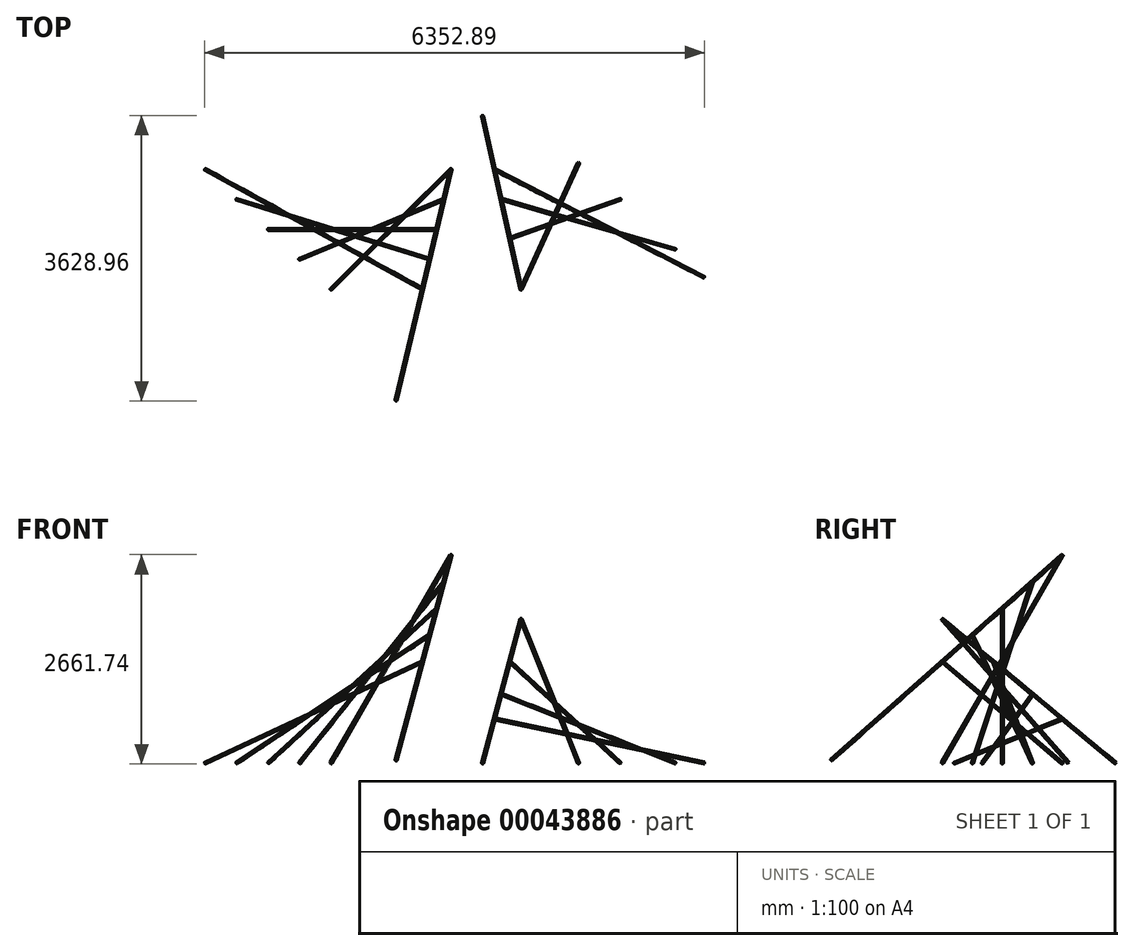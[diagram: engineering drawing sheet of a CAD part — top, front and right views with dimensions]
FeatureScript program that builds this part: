
annotation { "Feature Type Name" : "Feature", "Feature Type Description" : "" }
export const myFeature = defineFeature(function(context is Context, id is Id, definition is map)
    precondition{}
    {
        {
            var Q0;
            Q0=qCreatedBy(makeId("Front.planeOp"),FACE);
            var sketch = newSketch(context, id + "F0", { "sketchPlane" : qUnion([Q0])});
            skLineSegment(sketch, "E0", {"start": v(0, 0) * mm, "end": v(788.88, 2944.14) * mm});
            skSolve(sketch);
        }
        {
            var Q0;
            Q0=qCreatedBy(makeId("Front.planeOp"),FACE);
            cPlane(context, id + "F1", {"entities" : qUnion([Q0]), "cplaneType" : CPlaneType.OFFSET, "offset" : 1524 * mm, "oppositeDirection" : true, "width" : 152.4 * mm, "height" : 152.4 * mm});
        }
        {
            var Q0;
            Q0=qCreatedBy(id+"F1.planeOp",FACE);
            var sketch = newSketch(context, id + "F2", { "sketchPlane" : qUnion([Q0])});
            skLineSegment(sketch, "E1", {"start": v(0, 0) * mm, "end": v(788.88, 2944.14) * mm});
            skLineSegment(sketch, "E2", {"start": v(788.88, 2944.14) * mm, "end": v(522.39, 3015.55) * mm});
            skSolve(sketch);
        }
        {
            var Q0;
            Q0=qCreatedBy(id+"F1.planeOp",FACE);
            var sketch = newSketch(context, id + "F3", { "sketchPlane" : qUnion([Q0])});
            skLineSegment(sketch, "E3", {"start": v(788.88, 2944.14) * mm, "end": v(788.88, 0) * mm});
            skSolve(sketch);
        }
        {
            var Q0;
            Q0=qCreatedBy(id+"F1.planeOp",FACE);
            var sketch = newSketch(context, id + "F4", { "sketchPlane" : qUnion([Q0])});
            skLineSegment(sketch, "E4", {"start": v(788.88, 2944.14) * mm, "end": v(0, 0) * mm});
            skSolve(sketch);
        }
        {
            var Q0;
            Q0=qCreatedBy(id+"F1.planeOp",FACE);
            var sketch = newSketch(context, id + "F5", { "sketchPlane" : qUnion([Q0])});
            skLineSegment(sketch, "E5", {"start": v(345.16, 1288.14) * mm, "end": v(-2417.27, 0) * mm});
            skSolve(sketch);
        }
        {
            var Q0;
            Q0=qCreatedBy(makeId("Front.planeOp"),FACE);
            var sketch = newSketch(context, id + "F6", { "sketchPlane" : qUnion([Q0])});
            skLineSegment(sketch, "E6", {"start": v(-2417.27, 0) * mm, "end": v(345.16, 1288.14) * mm});
            skLineSegment(sketch, "E7", {"start": v(345.16, 1288.14) * mm, "end": v(246.93, 1498.78) * mm});
            skSolve(sketch);
        }
        {
            var Q0;
            Q0=qCreatedBy(makeId("Front.planeOp"),FACE);
            var sketch = newSketch(context, id + "F7", { "sketchPlane" : qUnion([Q0])});
            skLineSegment(sketch, "E8", {"start": v(707.3, 2639.65) * mm, "end": v(-816.7, 0) * mm});
            skSolve(sketch);
        }
        {
            var Q0;
            Q0=qCreatedBy(id+"F1.planeOp",FACE);
            var sketch = newSketch(context, id + "F8", { "sketchPlane" : qUnion([Q0])});
            skLineSegment(sketch, "E9", {"start": v(-816.7, 0) * mm, "end": v(707.3, 2639.65) * mm});
            skLineSegment(sketch, "E10", {"start": v(707.3, 2639.65) * mm, "end": v(435.48, 2796.58) * mm});
            skSolve(sketch);
        }
        {
            var Q0;
            Q0=qCreatedBy(makeId("Front.planeOp"),FACE);
            var sketch = newSketch(context, id + "F9", { "sketchPlane" : qUnion([Q0])});
            skLineSegment(sketch, "E11", {"start": v(345.16, 1288.14) * mm, "end": v(707.3, 2639.65) * mm});
            skPoint(sketch, "E12", {"position": v(526.22, 1963.9) * mm});
            skLineSegment(sketch, "E13", {"start": v(-816.7, 0) * mm, "end": v(-2417.27, 0) * mm});
            skPoint(sketch, "E14", {"position": v(-1616.99, 0) * mm});
            skSolve(sketch);
        }
        {
            var Q0;
            Q0=sQuery(id+"F9.wireOp",VERTEX,"E13.start");
            var Q1;
            Q1=sQuery(id+"F8.wireOp",VERTEX,"E10.start");
            var Q2;
            Q2=sQuery(id+"F8.wireOp",VERTEX,"E9.start");
            cPlane(context, id + "F10", {"entities" : qUnion([Q0, Q1, Q2]), "cplaneType" : CPlaneType.THREE_POINT, "offset" : 152.4 * mm, "width" : 152.4 * mm, "height" : 152.4 * mm});
        }
        {
            var Q0;
            Q0=qCreatedBy(id+"F10.planeOp",FACE);
            var sketch = newSketch(context, id + "F11", { "sketchPlane" : qUnion([Q0])});
            skLineSegment(sketch, "E15", {"start": v(0, -408.35) * mm, "end": v(1524, 2639.65) * mm});
            skSolve(sketch);
        }
        {
            var Q0;
            Q0=sQuery(id+"F6.wireOp",VERTEX,"E6.start");
            var Q1;
            Q1=sQuery(id+"F6.wireOp",VERTEX,"E7.start");
            var Q2;
            Q2=sQuery(id+"F5.wireOp",VERTEX,"E5.start");
            cPlane(context, id + "F12", {"entities" : qUnion([Q0, Q1, Q2]), "cplaneType" : CPlaneType.THREE_POINT, "offset" : 152.4 * mm, "width" : 152.4 * mm, "height" : 152.4 * mm});
        }
        {
            var Q0;
            Q0=qCreatedBy(id+"F12.planeOp",FACE);
            var sketch = newSketch(context, id + "F13", { "sketchPlane" : qUnion([Q0])});
            skLineSegment(sketch, "E16", {"start": v(-2190.8, -1524) * mm, "end": v(857.2, 0) * mm});
            skSolve(sketch);
        }
        {
            var Q0;
            Q0=qCreatedBy(makeId("Front.planeOp"),FACE);
            cPlane(context, id + "F14", {"entities" : qUnion([Q0]), "cplaneType" : CPlaneType.OFFSET, "offset" : 762 * mm, "oppositeDirection" : true, "width" : 152.4 * mm, "height" : 152.4 * mm});
        }
        {
            var Q0;
            Q0=qCreatedBy(id+"F14.planeOp",FACE);
            var sketch = newSketch(context, id + "F15", { "sketchPlane" : qUnion([Q0])});
            skLineSegment(sketch, "E17", {"start": v(-1616.99, 0) * mm, "end": v(526.22, 1963.9) * mm});
            skSolve(sketch);
        }
        {
            var Q0;
            Q0=qCreatedBy(makeId("Front.planeOp"),FACE);
            var sketch = newSketch(context, id + "F16", { "sketchPlane" : qUnion([Q0])});
            skLineSegment(sketch, "E18", {"start": v(526.22, 1963.9) * mm, "end": v(345.16, 1288.14) * mm});
            skLineSegment(sketch, "E19", {"start": v(526.22, 1963.9) * mm, "end": v(707.3, 2639.65) * mm});
            skLineSegment(sketch, "E20", {"start": v(-816.7, 0) * mm, "end": v(-1616.99, 0) * mm});
            skLineSegment(sketch, "E21", {"start": v(-1616.99, 0) * mm, "end": v(-2417.27, 0) * mm});
            skLineSegment(sketch, "E22", {"start": v(616.76, 2301.77) * mm, "end": v(-1216.85, 0) * mm});
            skLineSegment(sketch, "E23", {"start": v(-2017.13, 0) * mm, "end": v(435.69, 1626.02) * mm});
            skSolve(sketch);
        }
        {
            var Q0;
            Q0=sQuery(id+"F0.wireOp",VERTEX,"E0.start");
            var Q1;
            Q1=sQuery(id+"F16.wireOp",VERTEX,"E19.end");
            var Q2;
            Q2=sQuery(id+"F11.wireOp",VERTEX,"E15.end");
            cPlane(context, id + "F17", {"entities" : qUnion([Q0, Q1, Q2]), "cplaneType" : CPlaneType.THREE_POINT, "offset" : 152.4 * mm, "width" : 152.4 * mm, "height" : 152.4 * mm});
        }
        {
            var Q0;
            Q0=qCreatedBy(id+"F17.planeOp",FACE);
            var sketch = newSketch(context, id + "F18", { "sketchPlane" : qUnion([Q0])});
            skLineSegment(sketch, "E24", {"start": v(0, 0) * mm, "end": v(1524, 0) * mm});
            skLineSegment(sketch, "E25", {"start": v(0, 2382.97) * mm, "end": v(1524, 2382.97) * mm});
            skLineSegment(sketch, "E26", {"start": v(0, 1683.38) * mm, "end": v(1524, 1683.38) * mm});
            skLineSegment(sketch, "E27", {"start": v(0, 2382.97) * mm, "end": v(762, 2382.97) * mm});
            skLineSegment(sketch, "E28", {"start": v(762, 2382.97) * mm, "end": v(1524, 2382.97) * mm});
            skLineSegment(sketch, "E29", {"start": v(0, 1683.38) * mm, "end": v(762, 1683.38) * mm});
            skLineSegment(sketch, "E30", {"start": v(762, 1683.38) * mm, "end": v(1524, 1683.38) * mm});
            skPoint(sketch, "E31", {"position": v(381, 2382.97) * mm});
            skPoint(sketch, "E32", {"position": v(381, 1683.38) * mm});
            skPoint(sketch, "E33", {"position": v(1143, 2382.97) * mm});
            skPoint(sketch, "E34", {"position": v(1143, 1683.38) * mm});
            skSolve(sketch);
        }
        {
            var Q0;
            Q0=qCreatedBy(makeId("Top.planeOp"),FACE);
            var sketch = newSketch(context, id + "F19", { "sketchPlane" : qUnion([Q0])});
            skLineSegment(sketch, "E35", {"start": v(-2017.13, 0) * mm, "end": v(-2017.13, 1524) * mm});
            skLineSegment(sketch, "E36", {"start": v(-1216.85, 0) * mm, "end": v(-1216.85, 1524) * mm});
            skLineSegment(sketch, "E37", {"start": v(-2017.13, 762) * mm, "end": v(-2017.13, 1524) * mm});
            skLineSegment(sketch, "E38", {"start": v(-2017.13, 762) * mm, "end": v(-2017.13, 0) * mm});
            skLineSegment(sketch, "E39", {"start": v(-1216.85, 1524) * mm, "end": v(-1216.85, 762) * mm});
            skLineSegment(sketch, "E40", {"start": v(-1216.85, 762) * mm, "end": v(-1216.85, 0) * mm});
            skPoint(sketch, "E41", {"position": v(-1216.85, 381) * mm});
            skPoint(sketch, "E42", {"position": v(-2017.13, 381) * mm});
            skPoint(sketch, "E43", {"position": v(-2017.13, 1143) * mm});
            skPoint(sketch, "E44", {"position": v(-1216.85, 1143) * mm});
            skSolve(sketch);
        }
        {
            var Q0;
            Q0=sQuery(id+"F19.wireOp",VERTEX,"E43");
            var Q1;
            Q1=sQuery(id+"F18.wireOp",VERTEX,"E32");
            var Q2;
            Q2=sQuery(id+"F18.wireOp",VERTEX,"E34");
            cPlane(context, id + "F20", {"entities" : qUnion([Q0, Q1, Q2]), "cplaneType" : CPlaneType.THREE_POINT, "offset" : 152.4 * mm, "width" : 152.4 * mm, "height" : 152.4 * mm});
        }
        {
            var Q0;
            Q0=qCreatedBy(id+"F20.planeOp",FACE);
            var sketch = newSketch(context, id + "F21", { "sketchPlane" : qUnion([Q0])});
            skLineSegment(sketch, "E45", {"start": v(-1681.26, -1143) * mm, "end": v(1261.57, -381) * mm});
            skSolve(sketch);
        }
        {
            var Q0;
            Q0=sQuery(id+"F19.wireOp",VERTEX,"E41");
            var Q1;
            Q1=sQuery(id+"F18.wireOp",VERTEX,"E33");
            var Q2;
            Q2=sQuery(id+"F18.wireOp",VERTEX,"E31");
            cPlane(context, id + "F22", {"entities" : qUnion([Q0, Q1, Q2]), "cplaneType" : CPlaneType.THREE_POINT, "offset" : 152.4 * mm, "width" : 152.4 * mm, "height" : 152.4 * mm});
        }
        {
            var Q0;
            Q0=qCreatedBy(id+"F22.planeOp",FACE);
            var sketch = newSketch(context, id + "F23", { "sketchPlane" : qUnion([Q0])});
            skLineSegment(sketch, "E46", {"start": v(-381, -758.19) * mm, "end": v(-1143, 2184.64) * mm});
            skSolve(sketch);
        }
        {
            var Q0;
            Q0=sQuery(id+"F13.wireOp",VERTEX,"E16.end");
            var Q1;
            Q1=sQuery(id+"F11.wireOp",VERTEX,"E15.end");
            var Q2;
            Q2=sQuery(id+"F15.wireOp",VERTEX,"E17.start");
            cPlane(context, id + "F24", {"entities" : qUnion([Q0, Q1, Q2]), "cplaneType" : CPlaneType.THREE_POINT, "offset" : 152.4 * mm, "width" : 152.4 * mm, "height" : 152.4 * mm});
        }
        {
            var Q0;
            Q0=qCreatedBy(id+"F24.planeOp",FACE);
            var sketch = newSketch(context, id + "F25", { "sketchPlane" : qUnion([Q0])});
            skLineSegment(sketch, "E47", {"start": v(1378.45, -2734.5) * mm, "end": v(501.73, 1152.57) * mm});
            skSolve(sketch);
        }
        {
            var Q0;
            Q0=sQuery(id+"F11.wireOp",EDGE,"E15");
            cPlane(context, id + "F26", {"entities" : qUnion([Q0]), "cplaneType" : CPlaneType.MID_PLANE, "offset" : 152.4 * mm, "oppositeDirection" : true, "width" : 152.4 * mm, "height" : 152.4 * mm});
        }
        {
            var Q0;
            Q0=qCreatedBy(makeId("Top.planeOp"),FACE);
            var sketch = newSketch(context, id + "F27", { "sketchPlane" : qUnion([Q0])});
            skLineSegment(sketch, "E48", {"start": v(707.3, 1524) * mm, "end": v(345.16, 0) * mm});
            skLineSegment(sketch, "E49", {"start": v(707.3, 1524) * mm, "end": v(707.3, 0) * mm});
            skLineSegment(sketch, "E50.0", {"start": v(1469.3, 1524) * mm, "end": v(1469.3, 0) * mm});
            skLineSegment(sketch, "E51", {"start": v(1469.3, 1524) * mm, "end": v(1107.15, 0) * mm});
            skLineSegment(sketch, "E52", {"start": v(1469.3, 1524) * mm, "end": v(4234.33, 0) * mm});
            skSolve(sketch);
        }
        {
            var Q0;
            Q0=qCreatedBy(makeId("Front.planeOp"),FACE);
            var sketch = newSketch(context, id + "F28", { "sketchPlane" : qUnion([Q0])});
            skLineSegment(sketch, "E53", {"start": v(1469.3, 0) * mm, "end": v(4234.33, 0) * mm});
            skLineSegment(sketch, "E54.0", {"start": v(1469.3, 1828.8) * mm, "end": v(4234.33, 1828.8) * mm});
            skSolve(sketch);
        }
        {
            var Q0;
            Q0=qCreatedBy(makeId("Top.planeOp"),FACE);
            cPlane(context, id + "F29", {"entities" : qUnion([Q0]), "cplaneType" : CPlaneType.OFFSET, "offset" : 1828.8 * mm, "width" : 152.4 * mm, "height" : 152.4 * mm});
        }
        {
            var Q0;
            Q0=qCreatedBy(id+"F29.planeOp",FACE);
            var sketch = newSketch(context, id + "F30", { "sketchPlane" : qUnion([Q0])});
            skLineSegment(sketch, "E55", {"start": v(1469.3, 1524) * mm, "end": v(4234.33, 0) * mm});
            skSolve(sketch);
        }
        {
            var Q0;
            Q0=qCreatedBy(makeId("Front.planeOp"),FACE);
            var sketch = newSketch(context, id + "F31", { "sketchPlane" : qUnion([Q0])});
            skLineSegment(sketch, "E56", {"start": v(1107.15, 0) * mm, "end": v(1597.18, 1828.8) * mm});
            skLineSegment(sketch, "E57", {"start": v(1107.15, 0) * mm, "end": v(4221.7, 0) * mm});
            skLineSegment(sketch, "E58", {"start": v(4221.7, 0) * mm, "end": v(1257.92, 562.7) * mm});
            skLineSegment(sketch, "E59", {"start": v(3557.9, 0) * mm, "end": v(1352.16, 914.4) * mm});
            skLineSegment(sketch, "E60", {"start": v(2859.49, 0) * mm, "end": v(1452.5, 1288.87) * mm});
            skLineSegment(sketch, "E61", {"start": v(2259.2, 0) * mm, "end": v(1597.18, 1828.8) * mm});
            skSolve(sketch);
        }
        {
            var Q0;
            Q0=qCreatedBy(makeId("Top.planeOp"),FACE);
            var sketch = newSketch(context, id + "F32", { "sketchPlane" : qUnion([Q0])});
            skLineSegment(sketch, "E62", {"start": v(1597.18, 0) * mm, "end": v(1597.18, 1453.51) * mm});
            skSolve(sketch);
        }
        {
            var Q0;
            Q0=qCreatedBy(makeId("Top.planeOp"),FACE);
            var sketch = newSketch(context, id + "F33", { "sketchPlane" : qUnion([Q0])});
            skLineSegment(sketch, "E63", {"start": v(2259.2, 0) * mm, "end": v(1597.18, 1453.51) * mm});
            skSolve(sketch);
        }
        {
            var Q0;
            Q0=qCreatedBy(id+"F29.planeOp",FACE);
            var sketch = newSketch(context, id + "F34", { "sketchPlane" : qUnion([Q0])});
            skLineSegment(sketch, "E64", {"start": v(2259.2, 0) * mm, "end": v(1597.18, 1453.51) * mm});
            skSolve(sketch);
        }
        {
            var Q0;
            Q0=qCreatedBy(makeId("Top.planeOp"),FACE);
            var sketch = newSketch(context, id + "F35", { "sketchPlane" : qUnion([Q0])});
            skLineSegment(sketch, "E65", {"start": v(4221.7, 0) * mm, "end": v(4221.7, 1444.78) * mm});
            skLineSegment(sketch, "E66", {"start": v(1597.18, 1453.51) * mm, "end": v(4221.7, 1444.78) * mm});
            skSolve(sketch);
        }
        {
            var Q0;
            Q0=qCreatedBy(makeId("Top.planeOp"),FACE);
            var sketch = newSketch(context, id + "F36", { "sketchPlane" : qUnion([Q0])});
            skLineSegment(sketch, "E67", {"start": v(1257.92, 0) * mm, "end": v(4221.7, 1444.78) * mm});
            skSolve(sketch);
        }
        {
            var Q0;
            Q0=qCreatedBy(makeId("Top.planeOp"),FACE);
            var sketch = newSketch(context, id + "F37", { "sketchPlane" : qUnion([Q0])});
            skLineSegment(sketch, "E68", {"start": v(1257.92, 0) * mm, "end": v(1257.92, 1524) * mm});
            skLineSegment(sketch, "E69", {"start": v(1257.92, 1524) * mm, "end": v(4221.7, 0) * mm});
            skSolve(sketch);
        }
        {
            var Q0;
            Q0=qCreatedBy(id+"F29.planeOp",FACE);
            var sketch = newSketch(context, id + "F38", { "sketchPlane" : qUnion([Q0])});
            skLineSegment(sketch, "E70", {"start": v(1257.92, 1524) * mm, "end": v(4221.7, 0) * mm});
            skSolve(sketch);
        }
        {
            var Q0;
            Q0=sQuery(id+"F37.wireOp",VERTEX,"E69.end");
            var Q1;
            Q1=sQuery(id+"F37.wireOp",VERTEX,"E69.start");
            var Q2;
            Q2=sQuery(id+"F38.wireOp",VERTEX,"E70.start");
            cPlane(context, id + "F39", {"entities" : qUnion([Q0, Q1, Q2]), "cplaneType" : CPlaneType.THREE_POINT, "offset" : 152.4 * mm, "width" : 152.4 * mm, "height" : 152.4 * mm});
        }
        {
            var Q0;
            Q0=qCreatedBy(id+"F39.planeOp",FACE);
            var sketch = newSketch(context, id + "F40", { "sketchPlane" : qUnion([Q0])});
            skLineSegment(sketch, "E71", {"start": v(3417.44, 0) * mm, "end": v(421.77, 562.4) * mm});
            skSolve(sketch);
        }
        {
            var Q0;
            Q0=qCreatedBy(makeId("Top.planeOp"),FACE);
            var sketch = newSketch(context, id + "F41", { "sketchPlane" : qUnion([Q0])});
            skLineSegment(sketch, "E72", {"start": v(2259.2, 0) * mm, "end": v(2259.2, 1451.31) * mm});
            skSolve(sketch);
        }
        {
            var Q0;
            Q0=sQuery(id+"F41.wireOp",VERTEX,"E72.end");
            var Q1;
            Q1=sQuery(id+"F31.wireOp",VERTEX,"E61.end");
            var Q2;
            Q2=sQuery(id+"F32.wireOp",VERTEX,"E62.start");
            cPlane(context, id + "F42", {"entities" : qUnion([Q0, Q1, Q2]), "cplaneType" : CPlaneType.THREE_POINT, "offset" : 152.4 * mm, "width" : 152.4 * mm, "height" : 152.4 * mm});
        }
        {
            var Q0;
            Q0=qCreatedBy(id+"F42.planeOp",FACE);
            var sketch = newSketch(context, id + "F43", { "sketchPlane" : qUnion([Q0])});
            skLineSegment(sketch, "E73", {"start": v(-2425.54, 0) * mm, "end": v(-662.85, 1828.8) * mm});
            skSolve(sketch);
        }
        {
            var Q0;
            Q0=qCreatedBy(makeId("Top.planeOp"),FACE);
            var sketch = newSketch(context, id + "F44", { "sketchPlane" : qUnion([Q0])});
            skLineSegment(sketch, "E74", {"start": v(1107.15, 0) * mm, "end": v(1107.15, 1524) * mm});
            skLineSegment(sketch, "E75", {"start": v(1257.92, 0) * mm, "end": v(1257.92, 1524) * mm});
            skLineSegment(sketch, "E76", {"start": v(1352.16, 0) * mm, "end": v(1352.16, 1143) * mm});
            skLineSegment(sketch, "E77", {"start": v(1452.5, 0) * mm, "end": v(1452.5, 381) * mm});
            skLineSegment(sketch, "E78", {"start": v(3557.9, 0) * mm, "end": v(3557.9, 508) * mm});
            skLineSegment(sketch, "E79", {"start": v(2859.49, 0) * mm, "end": v(2859.49, 1143) * mm});
            skLineSegment(sketch, "E80", {"start": v(3557.9, 508) * mm, "end": v(1352.16, 1143) * mm});
            skLineSegment(sketch, "E81", {"start": v(2859.49, 1143) * mm, "end": v(1452.5, 381) * mm});
            skSolve(sketch);
        }
        {
            var Q0;
            Q0=qCreatedBy(id+"F29.planeOp",FACE);
            var sketch = newSketch(context, id + "F45", { "sketchPlane" : qUnion([Q0])});
            skLineSegment(sketch, "E82", {"start": v(2859.49, 1143) * mm, "end": v(1452.5, 381) * mm});
            skLineSegment(sketch, "E83", {"start": v(3557.9, 508) * mm, "end": v(1352.16, 1143) * mm});
            skSolve(sketch);
        }
        {
            var Q0;
            Q0=sQuery(id+"F45.wireOp",VERTEX,"E82.start");
            var Q1;
            Q1=sQuery(id+"F45.wireOp",VERTEX,"E82.end");
            var Q2;
            Q2=sQuery(id+"F44.wireOp",VERTEX,"E81.end");
            cPlane(context, id + "F46", {"entities" : qUnion([Q0, Q1, Q2]), "cplaneType" : CPlaneType.THREE_POINT, "offset" : 152.4 * mm, "width" : 152.4 * mm, "height" : 152.4 * mm});
        }
        {
            var Q0;
            Q0=sQuery(id+"F31.wireOp",VERTEX,"E60.end");
            var Q1;
            Q1=qCreatedBy(makeId("Top.planeOp"),FACE);
            cPlane(context, id + "F47", {"entities" : qUnion([Q0, Q1]), "cplaneType" : CPlaneType.PLANE_POINT, "offset" : 152.4 * mm, "width" : 152.4 * mm, "height" : 152.4 * mm});
        }
        {
            var Q0;
            Q0=qCreatedBy(id+"F47.planeOp",FACE);
            var sketch = newSketch(context, id + "F48", { "sketchPlane" : qUnion([Q0])});
            skLineSegment(sketch, "E84", {"start": v(1452.5, 0) * mm, "end": v(1452.5, 381) * mm});
            skSolve(sketch);
        }
        {
            var Q0;
            Q0=qCreatedBy(id+"F46.planeOp",FACE);
            var sketch = newSketch(context, id + "F49", { "sketchPlane" : qUnion([Q0])});
            skLineSegment(sketch, "E85", {"start": v(-3058.74, 0) * mm, "end": v(-1458.66, 1288.87) * mm});
            skSolve(sketch);
        }
        {
            var Q0;
            Q0=sQuery(id+"F31.wireOp",VERTEX,"E59.end");
            var Q1;
            Q1=qCreatedBy(makeId("Top.planeOp"),FACE);
            cPlane(context, id + "F50", {"entities" : qUnion([Q0, Q1]), "cplaneType" : CPlaneType.PLANE_POINT, "offset" : 152.4 * mm, "width" : 152.4 * mm, "height" : 152.4 * mm});
        }
        {
            var Q0;
            Q0=qCreatedBy(id+"F50.planeOp",FACE);
            var sketch = newSketch(context, id + "F51", { "sketchPlane" : qUnion([Q0])});
            skLineSegment(sketch, "E86", {"start": v(1352.16, 1143) * mm, "end": v(1352.16, 0) * mm});
            skSolve(sketch);
        }
        {
            var Q0;
            Q0=sQuery(id+"F44.wireOp",VERTEX,"E80.start");
            var Q1;
            Q1=sQuery(id+"F44.wireOp",VERTEX,"E80.end");
            var Q2;
            Q2=sQuery(id+"F51.wireOp",VERTEX,"E86.start");
            cPlane(context, id + "F52", {"entities" : qUnion([Q0, Q1, Q2]), "cplaneType" : CPlaneType.THREE_POINT, "offset" : 152.4 * mm, "width" : 152.4 * mm, "height" : 152.4 * mm});
        }
        {
            var Q0;
            Q0=qCreatedBy(id+"F52.planeOp",FACE);
            var sketch = newSketch(context, id + "F53", { "sketchPlane" : qUnion([Q0])});
            skLineSegment(sketch, "E87", {"start": v(3278.5, 0) * mm, "end": v(983.18, 914.4) * mm});
            skSolve(sketch);
        }
        {
            var Q0;
            Q0=sQuery(id+"F31.wireOp",VERTEX,"E56.start");
            var Q1;
            Q1=sQuery(id+"F43.wireOp",VERTEX,"E73.end");
            var Q2;
            Q2=sQuery(id+"F40.wireOp",VERTEX,"E71.end");
            cPlane(context, id + "F54", {"entities" : qUnion([Q0, Q1, Q2]), "cplaneType" : CPlaneType.THREE_POINT, "offset" : 152.4 * mm, "width" : 152.4 * mm, "height" : 152.4 * mm});
        }
        {
            var Q0;
            Q0=qCreatedBy(id+"F54.planeOp",FACE);
            var sketch = newSketch(context, id + "F55", { "sketchPlane" : qUnion([Q0])});
            skLineSegment(sketch, "E88", {"start": v(0.05, 2179.86) * mm, "end": v(2200.88, 286.55) * mm});
            skLineSegment(sketch, "E89", {"start": v(0.05, 286.55) * mm, "end": v(2200.88, 286.55) * mm});
            skSolve(sketch);
        }
        {
            var Q0;
            Q0=sQuery(id+"F49.wireOp",VERTEX,"E85.end");
            var Q1;
            Q1=qCreatedBy(makeId("Top.planeOp"),FACE);
            cPlane(context, id + "F56", {"entities" : qUnion([Q0, Q1]), "cplaneType" : CPlaneType.PLANE_POINT, "offset" : 152.4 * mm, "width" : 152.4 * mm, "height" : 152.4 * mm});
        }
        {
            var Q0;
            Q0=qCreatedBy(id+"F56.planeOp",FACE);
            var sketch = newSketch(context, id + "F57", { "sketchPlane" : qUnion([Q0])});
            skLineSegment(sketch, "E90", {"start": v(1452.5, 381) * mm, "end": v(1452.5, 649.9) * mm});
            skSolve(sketch);
        }
        {
            var Q0;
            Q0=sQuery(id+"F57.wireOp",VERTEX,"E90.end");
            var Q1;
            Q1=qCreatedBy(makeId("Front.planeOp"),FACE);
            cPlane(context, id + "F58", {"entities" : qUnion([Q0, Q1]), "cplaneType" : CPlaneType.PLANE_POINT, "offset" : 152.4 * mm, "width" : 152.4 * mm, "height" : 152.4 * mm});
        }
        {
            var Q0;
            Q0=qCreatedBy(id+"F58.planeOp",FACE);
            var sketch = newSketch(context, id + "F59", { "sketchPlane" : qUnion([Q0])});
            skLineSegment(sketch, "E91", {"start": v(1452.5, 1288.87) * mm, "end": v(1452.5, 0) * mm});
            skSolve(sketch);
        }
        {
            var Q0;
            Q0=sQuery(id+"F59.wireOp",VERTEX,"E91.start");
            var Q1;
            Q1=sQuery(id+"F59.wireOp",VERTEX,"E91.end");
            var Q2;
            Q2=sQuery(id+"F49.wireOp",VERTEX,"E85.start");
            cPlane(context, id + "F60", {"entities" : qUnion([Q0, Q1, Q2]), "cplaneType" : CPlaneType.THREE_POINT, "offset" : 152.4 * mm, "width" : 152.4 * mm, "height" : 152.4 * mm});
        }
        {
            var Q0;
            Q0=qCreatedBy(id+"F60.planeOp",FACE);
            var sketch = newSketch(context, id + "F61", { "sketchPlane" : qUnion([Q0])});
            skLineSegment(sketch, "E92", {"start": v(-1585.7, 1288.87) * mm, "end": v(-3076.6, 0) * mm});
            skSolve(sketch);
        }
        {
            var Q0;
            Q0=sQuery(id+"F25.wireOp",EDGE,"E47");
            var Q1;
            Q1=sQuery(id+"F25.wireOp",VERTEX,"E47.start");
            cPlane(context, id + "F62", {"entities" : qUnion([Q0, Q1]), "cplaneType" : CPlaneType.LINE_POINT, "offset" : 152.4 * mm, "width" : 152.4 * mm, "height" : 152.4 * mm});
        }
        {
            var Q0;
            Q0=qCreatedBy(id+"F62.planeOp",FACE);
            var sketch = newSketch(context, id + "F63", { "sketchPlane" : qUnion([Q0])});
            skCircle(sketch, "E93", {"center": v(190.23, 963.76) * mm, "radius": 12.7 * mm});
            skSolve(sketch);
        }
        {
            var Q0;
            Q0=makeQuery(id+"F63.imprint","IMPRINT",FACE,{"disambiguationData":[TD([[makeQuery(id+"F63.imprint","IMPRINT",EDGE,{"derivedFrom":sQuery(id+"F63.wireOp",EDGE,"E93")}),1.0]])]});
            var Q1;
            Q1=sQuery(id+"F25.wireOp",EDGE,"E47");
            sweep(context, id + "F64", {"profiles" : qUnion([Q0]), "path" : qUnion([Q1])});
        }
        {
            var Q0;
            Q0=sQuery(id+"F55.wireOp",EDGE,"E88");
            cPlane(context, id + "F65", {"entities" : qUnion([Q0]), "cplaneType" : CPlaneType.LINE_ANGLE, "offset" : 152.4 * mm, "angle" : 90 * degree, "width" : 152.4 * mm, "height" : 152.4 * mm});
        }
        {
            var Q0;
            Q0=qCreatedBy(id+"F65.planeOp",FACE);
            var sketch = newSketch(context, id + "F66", { "sketchPlane" : qUnion([Q0])});
            skLineSegment(sketch, "E94", {"start": v(-180.25, 1991.68) * mm, "end": v(2039.35, 120.41) * mm});
            skSolve(sketch);
        }
        {
            var Q0;
            Q0=sQuery(id+"F53.wireOp",EDGE,"E87");
            cPlane(context, id + "F67", {"entities" : qUnion([Q0]), "cplaneType" : CPlaneType.LINE_ANGLE, "offset" : 152.4 * mm, "angle" : 0 * degree, "width" : 152.4 * mm, "height" : 152.4 * mm});
        }
        {
            var Q0;
            Q0=qCreatedBy(id+"F67.planeOp",FACE);
            var sketch = newSketch(context, id + "F68", { "sketchPlane" : qUnion([Q0])});
            skLineSegment(sketch, "E95", {"start": v(3278.5, 0) * mm, "end": v(972.7, 876.59) * mm});
            skSolve(sketch);
        }
        {
            var Q0;
            Q0=sQuery(id+"F13.wireOp",EDGE,"E16");
            var Q1;
            Q1=sQuery(id+"F13.wireOp",VERTEX,"E16.end");
            cPlane(context, id + "F69", {"entities" : qUnion([Q0, Q1]), "cplaneType" : CPlaneType.LINE_POINT, "offset" : 152.4 * mm, "width" : 152.4 * mm, "height" : 152.4 * mm});
        }
        {
            var Q0;
            Q0=qCreatedBy(id+"F69.planeOp",FACE);
            var sketch = newSketch(context, id + "F70", { "sketchPlane" : qUnion([Q0])});
            skCircle(sketch, "E96", {"center": v(383.36, 1021.58) * mm, "radius": 12.7 * mm});
            skSolve(sketch);
        }
        {
            var Q0;
            Q0=makeQuery(id+"F70.imprint","IMPRINT",FACE,{"disambiguationData":[TD([[makeQuery(id+"F70.imprint","IMPRINT",EDGE,{"derivedFrom":sQuery(id+"F70.wireOp",EDGE,"E96")}),1.0]])]});
            var Q1;
            Q1=sQuery(id+"F13.wireOp",EDGE,"E16");
            sweep(context, id + "F71", {"profiles" : qUnion([Q0]), "path" : qUnion([Q1])});
        }
        {
            var Q0;
            Q0=sQuery(id+"F21.wireOp",EDGE,"E45");
            var Q1;
            Q1=sQuery(id+"F21.wireOp",VERTEX,"E45.end");
            cPlane(context, id + "F72", {"entities" : qUnion([Q0, Q1]), "cplaneType" : CPlaneType.LINE_POINT, "offset" : 152.4 * mm, "width" : 152.4 * mm, "height" : 152.4 * mm});
        }
        {
            var Q0;
            Q0=qCreatedBy(id+"F72.planeOp",FACE);
            var sketch = newSketch(context, id + "F73", { "sketchPlane" : qUnion([Q0])});
            skCircle(sketch, "E97", {"center": v(685.07, 1114.53) * mm, "radius": 12.7 * mm});
            skSolve(sketch);
        }
        {
            var Q0;
            Q0=makeQuery(id+"F73.imprint","IMPRINT",FACE,{"disambiguationData":[TD([[makeQuery(id+"F73.imprint","IMPRINT",EDGE,{"derivedFrom":sQuery(id+"F73.wireOp",EDGE,"E97")}),1.0]])]});
            var Q1;
            Q1=sQuery(id+"F21.wireOp",EDGE,"E45");
            sweep(context, id + "F74", {"profiles" : qUnion([Q0]), "path" : qUnion([Q1])});
        }
        {
            var Q0;
            Q0=sQuery(id+"F15.wireOp",EDGE,"E17");
            var Q1;
            Q1=sQuery(id+"F15.wireOp",VERTEX,"E17.end");
            cPlane(context, id + "F75", {"entities" : qUnion([Q0, Q1]), "cplaneType" : CPlaneType.LINE_POINT, "offset" : 152.4 * mm, "width" : 152.4 * mm, "height" : 152.4 * mm});
        }
        {
            var Q0;
            Q0=qCreatedBy(id+"F75.planeOp",FACE);
            var sketch = newSketch(context, id + "F76", { "sketchPlane" : qUnion([Q0])});
            skCircle(sketch, "E98", {"center": v(762, 1092.42) * mm, "radius": 12.7 * mm});
            skSolve(sketch);
        }
        {
            var Q0;
            Q0=makeQuery(id+"F76.imprint","IMPRINT",FACE,{"disambiguationData":[TD([[makeQuery(id+"F76.imprint","IMPRINT",EDGE,{"derivedFrom":sQuery(id+"F76.wireOp",EDGE,"E98")}),1.0]])]});
            var Q1;
            Q1=sQuery(id+"F15.wireOp",EDGE,"E17");
            sweep(context, id + "F77", {"profiles" : qUnion([Q0]), "path" : qUnion([Q1])});
        }
        {
            var Q0;
            Q0=sQuery(id+"F23.wireOp",EDGE,"E46");
            var Q1;
            Q1=sQuery(id+"F23.wireOp",VERTEX,"E46.end");
            cPlane(context, id + "F78", {"entities" : qUnion([Q0, Q1]), "cplaneType" : CPlaneType.LINE_POINT, "offset" : 152.4 * mm, "width" : 152.4 * mm, "height" : 152.4 * mm});
        }
        {
            var Q0;
            Q0=qCreatedBy(id+"F78.planeOp",FACE);
            var sketch = newSketch(context, id + "F79", { "sketchPlane" : qUnion([Q0])});
            skCircle(sketch, "E99", {"center": v(-1042.79, 361.7) * mm, "radius": 12.7 * mm});
            skSolve(sketch);
        }
        {
            var Q0;
            Q0=makeQuery(id+"F79.imprint","IMPRINT",FACE,{"disambiguationData":[TD([[makeQuery(id+"F79.imprint","IMPRINT",EDGE,{"derivedFrom":sQuery(id+"F79.wireOp",EDGE,"E99")}),1.0]])]});
            var Q1;
            Q1=sQuery(id+"F23.wireOp",EDGE,"E46");
            sweep(context, id + "F80", {"profiles" : qUnion([Q0]), "path" : qUnion([Q1])});
        }
        {
            var Q0;
            Q0=sQuery(id+"F11.wireOp",EDGE,"E15");
            var Q1;
            Q1=sQuery(id+"F11.wireOp",VERTEX,"E15.end");
            cPlane(context, id + "F81", {"entities" : qUnion([Q0, Q1]), "cplaneType" : CPlaneType.LINE_POINT, "offset" : 152.4 * mm, "width" : 152.4 * mm, "height" : 152.4 * mm});
        }
        {
            var Q0;
            Q0=qCreatedBy(id+"F81.planeOp",FACE);
            var sketch = newSketch(context, id + "F82", { "sketchPlane" : qUnion([Q0])});
            skCircle(sketch, "E100", {"center": v(-730.49, 0) * mm, "radius": 12.7 * mm});
            skSolve(sketch);
        }
        {
            var Q0;
            Q0=makeQuery(id+"F82.imprint","IMPRINT",FACE,{"disambiguationData":[TD([[makeQuery(id+"F82.imprint","IMPRINT",EDGE,{"derivedFrom":sQuery(id+"F82.wireOp",EDGE,"E100")}),1.0]])]});
            var Q1;
            Q1=sQuery(id+"F11.wireOp",EDGE,"E15");
            sweep(context, id + "F83", {"profiles" : qUnion([Q0]), "path" : qUnion([Q1])});
        }
        {
            var Q0;
            Q0=sQuery(id+"F66.wireOp",EDGE,"E94");
            var Q1;
            Q1=sQuery(id+"F43.wireOp",VERTEX,"E73.end");
            cPlane(context, id + "F84", {"entities" : qUnion([Q0, Q1]), "cplaneType" : CPlaneType.LINE_POINT, "offset" : 152.4 * mm, "width" : 152.4 * mm, "height" : 152.4 * mm});
        }
        {
            var Q0;
            Q0=qCreatedBy(id+"F84.planeOp",FACE);
            var sketch = newSketch(context, id + "F85", { "sketchPlane" : qUnion([Q0])});
            skCircle(sketch, "E101", {"center": v(-1377.03, 1406.55) * mm, "radius": 12.7 * mm});
            skSolve(sketch);
        }
        {
            var Q0;
            Q0=makeQuery(id+"F85.imprint","IMPRINT",FACE,{"disambiguationData":[TD([[makeQuery(id+"F85.imprint","IMPRINT",EDGE,{"derivedFrom":sQuery(id+"F85.wireOp",EDGE,"E101")}),1.0]])]});
            var Q1;
            Q1=sQuery(id+"F66.wireOp",EDGE,"E94");
            sweep(context, id + "F86", {"profiles" : qUnion([Q0]), "path" : qUnion([Q1])});
        }
        {
            var Q0;
            Q0=sQuery(id+"F43.wireOp",EDGE,"E73");
            var Q1;
            Q1=sQuery(id+"F43.wireOp",VERTEX,"E73.end");
            cPlane(context, id + "F87", {"entities" : qUnion([Q0, Q1]), "cplaneType" : CPlaneType.LINE_POINT, "offset" : 152.4 * mm, "width" : 152.4 * mm, "height" : 152.4 * mm});
        }
        {
            var Q0;
            Q0=qCreatedBy(id+"F87.planeOp",FACE);
            var sketch = newSketch(context, id + "F88", { "sketchPlane" : qUnion([Q0])});
            skCircle(sketch, "E102", {"center": v(1925.51, 1205.77) * mm, "radius": 12.7 * mm});
            skSolve(sketch);
        }
        {
            var Q0;
            Q0=makeQuery(id+"F88.imprint","IMPRINT",FACE,{"disambiguationData":[TD([[makeQuery(id+"F88.imprint","IMPRINT",EDGE,{"derivedFrom":sQuery(id+"F88.wireOp",EDGE,"E102")}),1.0]])]});
            var Q1;
            Q1=sQuery(id+"F43.wireOp",EDGE,"E73");
            sweep(context, id + "F89", {"profiles" : qUnion([Q0]), "path" : qUnion([Q1])});
        }
        {
            var Q0;
            Q0=sQuery(id+"F61.wireOp",EDGE,"E92");
            var Q1;
            Q1=sQuery(id+"F61.wireOp",VERTEX,"E92.start");
            cPlane(context, id + "F90", {"entities" : qUnion([Q0, Q1]), "cplaneType" : CPlaneType.LINE_POINT, "offset" : 152.4 * mm, "width" : 152.4 * mm, "height" : 152.4 * mm});
        }
        {
            var Q0;
            Q0=qCreatedBy(id+"F90.planeOp",FACE);
            var sketch = newSketch(context, id + "F91", { "sketchPlane" : qUnion([Q0])});
            skCircle(sketch, "E103", {"center": v(579.08, 1931.52) * mm, "radius": 12.7 * mm});
            skSolve(sketch);
        }
        {
            var Q0;
            Q0=makeQuery(id+"F91.imprint","IMPRINT",FACE,{"disambiguationData":[TD([[makeQuery(id+"F91.imprint","IMPRINT",EDGE,{"derivedFrom":sQuery(id+"F91.wireOp",EDGE,"E103")}),1.0]])]});
            var Q1;
            Q1=sQuery(id+"F61.wireOp",EDGE,"E92");
            sweep(context, id + "F92", {"profiles" : qUnion([Q0]), "path" : qUnion([Q1])});
        }
        {
            var Q0;
            Q0=sQuery(id+"F68.wireOp",EDGE,"E95");
            var Q1;
            Q1=sQuery(id+"F68.wireOp",VERTEX,"E95.end");
            cPlane(context, id + "F93", {"entities" : qUnion([Q0, Q1]), "cplaneType" : CPlaneType.LINE_POINT, "offset" : 152.4 * mm, "width" : 152.4 * mm, "height" : 152.4 * mm});
        }
        {
            var Q0;
            Q0=qCreatedBy(id+"F93.planeOp",FACE);
            var sketch = newSketch(context, id + "F94", { "sketchPlane" : qUnion([Q0])});
            skCircle(sketch, "E104", {"center": v(-1346.26, 1308.83) * mm, "radius": 12.7 * mm});
            skSolve(sketch);
        }
        {
            var Q0;
            Q0=makeQuery(id+"F94.imprint","IMPRINT",FACE,{"disambiguationData":[TD([[makeQuery(id+"F94.imprint","IMPRINT",EDGE,{"derivedFrom":sQuery(id+"F94.wireOp",EDGE,"E104")}),1.0]])]});
            var Q1;
            Q1=sQuery(id+"F68.wireOp",EDGE,"E95");
            sweep(context, id + "F95", {"profiles" : qUnion([Q0]), "path" : qUnion([Q1])});
        }
        {
            var Q0;
            Q0=sQuery(id+"F40.wireOp",EDGE,"E71");
            var Q1;
            Q1=sQuery(id+"F40.wireOp",VERTEX,"E71.end");
            cPlane(context, id + "F96", {"entities" : qUnion([Q0, Q1]), "cplaneType" : CPlaneType.LINE_POINT, "offset" : 152.4 * mm, "width" : 152.4 * mm, "height" : 152.4 * mm});
        }
        {
            var Q0;
            Q0=qCreatedBy(id+"F96.planeOp",FACE);
            var sketch = newSketch(context, id + "F97", { "sketchPlane" : qUnion([Q0])});
            skCircle(sketch, "E105", {"center": v(-1862.37, 810.1) * mm, "radius": 12.7 * mm});
            skSolve(sketch);
        }
        {
            var Q0;
            Q0=makeQuery(id+"F97.imprint","IMPRINT",FACE,{"disambiguationData":[TD([[makeQuery(id+"F97.imprint","IMPRINT",EDGE,{"derivedFrom":sQuery(id+"F97.wireOp",EDGE,"E105")}),1.0]])]});
            var Q1;
            Q1=sQuery(id+"F40.wireOp",EDGE,"E71");
            sweep(context, id + "F98", {"profiles" : qUnion([Q0]), "path" : qUnion([Q1])});
        }
    });
